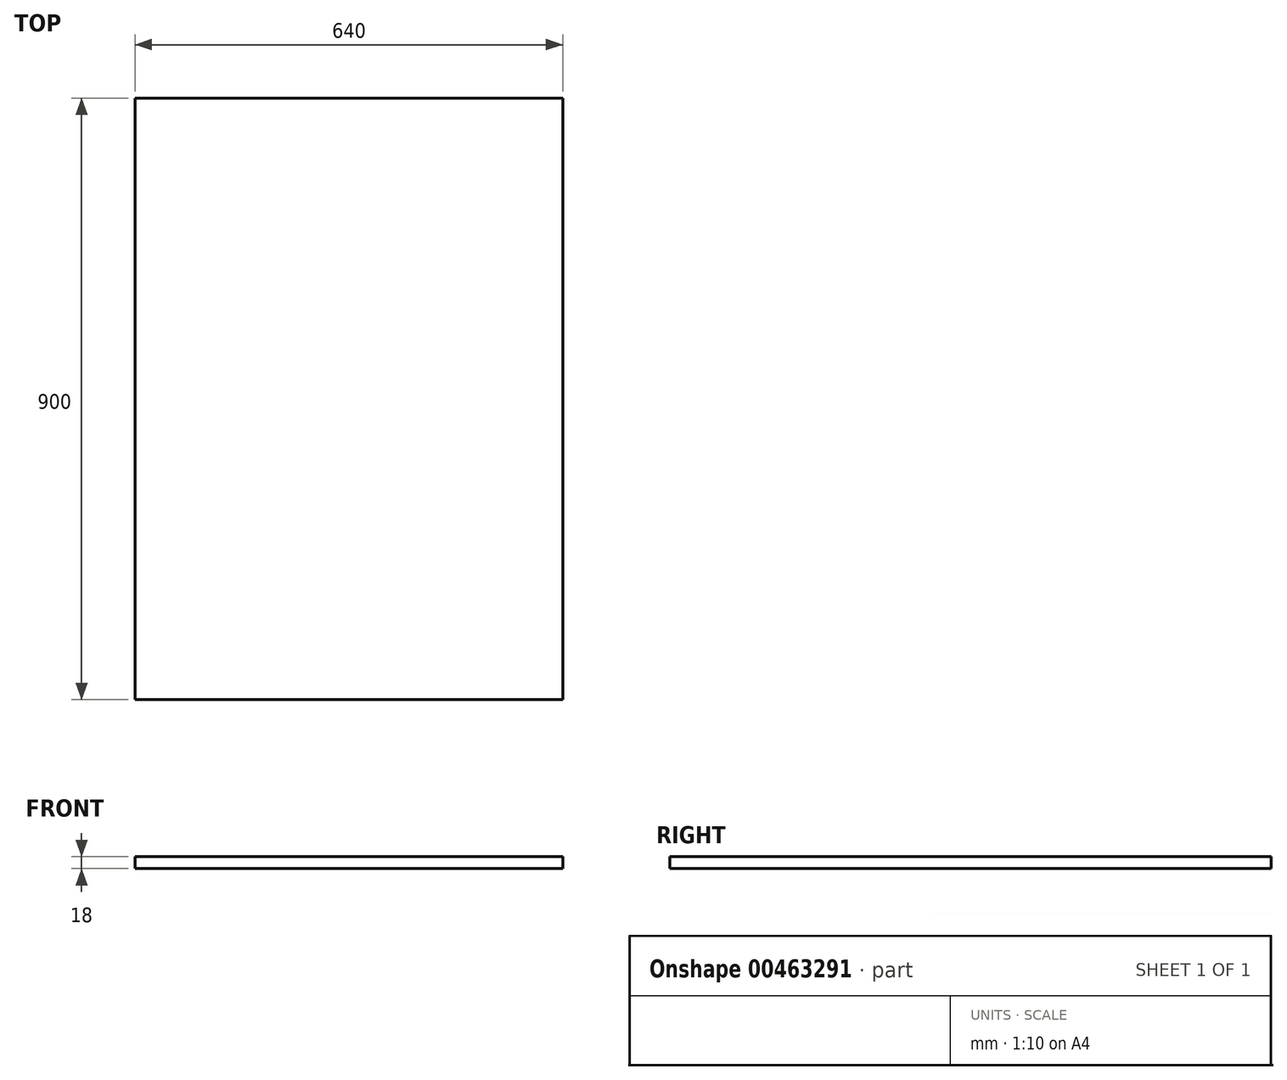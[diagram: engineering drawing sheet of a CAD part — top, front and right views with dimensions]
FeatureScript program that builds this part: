
annotation { "Feature Type Name" : "Feature", "Feature Type Description" : "" }
export const myFeature = defineFeature(function(context is Context, id is Id, definition is map)
    precondition{}
    {
        {
            var Q0;
            Q0=qCreatedBy(makeId("Top.planeOp"),FACE);
            var sketch = newSketch(context, id + "F0", { "sketchPlane" : qUnion([Q0])});
            skLineSegment(sketch, "E0.bottom", {"start": v(0, 0) * mm, "end": v(640, 0) * mm});
            skLineSegment(sketch, "E0.top", {"start": v(0, 900) * mm, "end": v(640, 900) * mm});
            skLineSegment(sketch, "E0.left", {"start": v(0, 0) * mm, "end": v(0, 900) * mm});
            skLineSegment(sketch, "E0.right", {"start": v(640, 0) * mm, "end": v(640, 900) * mm});
            skSolve(sketch);
        }
        {
            var Q0;
            Q0 = qSketchRegion(id + "F0", true);
            extrude(context, id + "F1", {"entities" : qUnion([Q0]), "depth" : 18 * mm});
        }
    });
